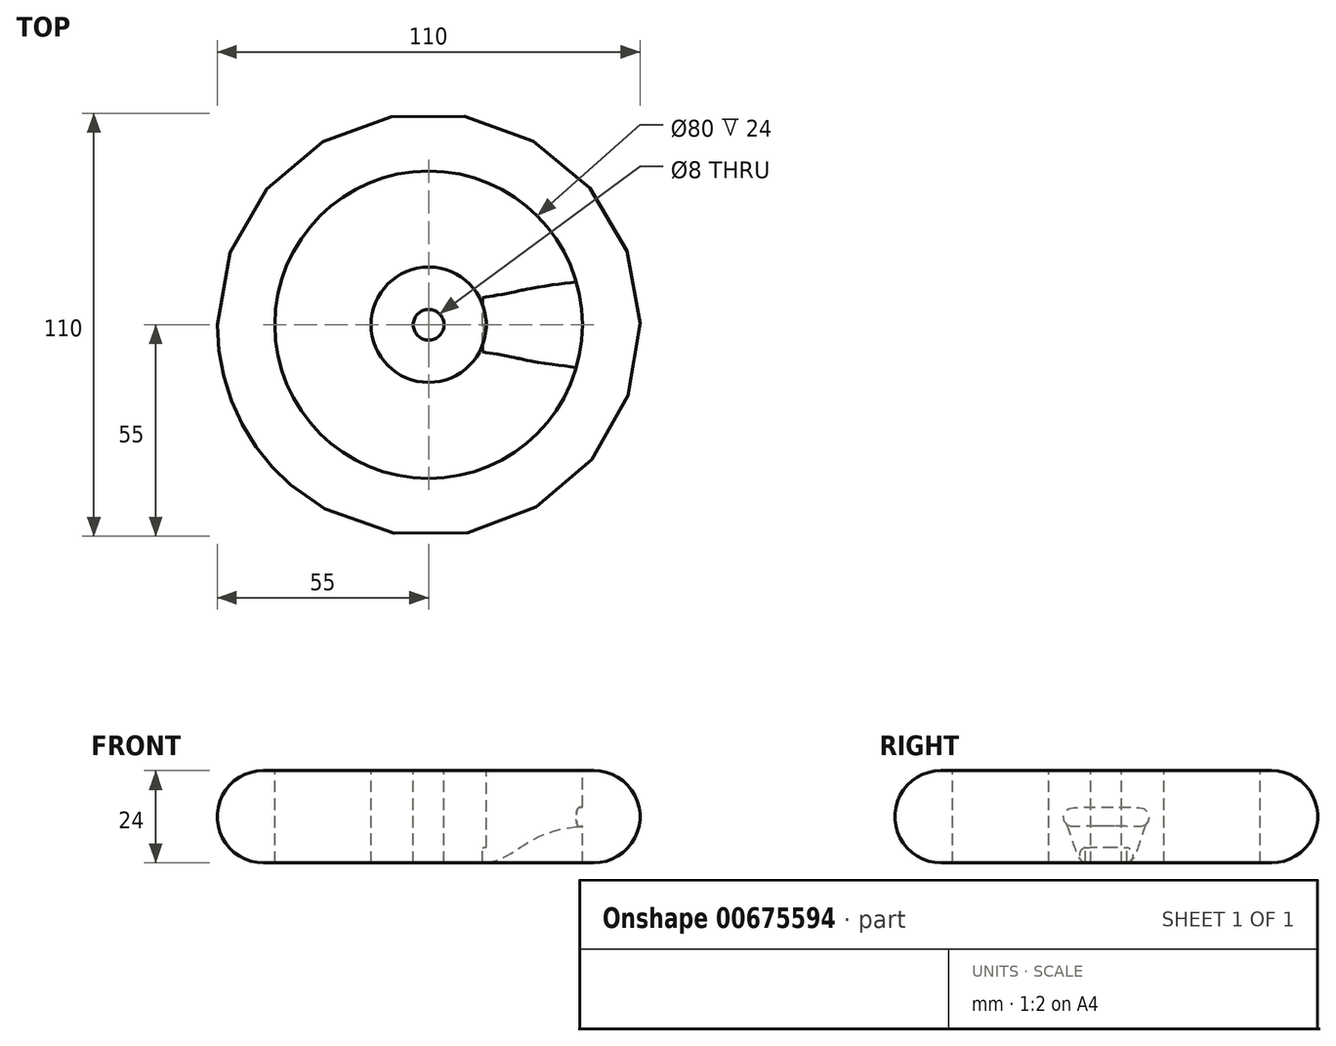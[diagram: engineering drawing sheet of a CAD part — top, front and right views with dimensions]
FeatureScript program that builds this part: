
annotation { "Feature Type Name" : "Feature", "Feature Type Description" : "" }
export const myFeature = defineFeature(function(context is Context, id is Id, definition is map)
    precondition{}
    {
        {
            var Q0;
            Q0=qCreatedBy(makeId("Top.planeOp"),FACE);
            var sketch = newSketch(context, id + "F0", { "sketchPlane" : qUnion([Q0])});
            skCircle(sketch, "E0", {"center": v(0, 0) * mm, "radius": 40 * mm});
            skSolve(sketch);
        }
        {
            var Q0;
            Q0=qCreatedBy(makeId("Front.planeOp"),FACE);
            var sketch = newSketch(context, id + "F1", { "sketchPlane" : qUnion([Q0])});
            skArc(sketch, "E1", {"start": v(-43, 12) * mm, "mid": v(-55, 0) * mm, "end": v(-43, -12) * mm});
            skLineSegment(sketch, "E2", {"start": v(-43, 12) * mm, "end": v(-40, 12) * mm});
            skLineSegment(sketch, "E3", {"start": v(-40, 12) * mm, "end": v(-40, -12) * mm});
            skLineSegment(sketch, "E4", {"start": v(-40, -12) * mm, "end": v(-43, -12) * mm});
            skSolve(sketch);
        }
        {
            var Q0;
            Q0 = qSketchRegion(id + "F1", true);
            var Q1;
            Q1=sQuery(id+"F0.wireOp",EDGE,"E0");
            sweep(context, id + "F2", {"profiles" : qUnion([Q0]), "path" : qUnion([Q1])});
        }
        {
            var Q0;
            Q0=qCreatedBy(makeId("Right.planeOp"),FACE);
            cPlane(context, id + "F3", {"entities" : qUnion([Q0]), "cplaneType" : CPlaneType.OFFSET, "offset" : 40 * mm, "width" : 150 * mm, "height" : 150 * mm});
        }
        {
            var Q0;
            Q0=qCreatedBy(id+"F3.planeOp",FACE);
            var sketch = newSketch(context, id + "F4", { "sketchPlane" : qUnion([Q0])});
            skLineSegment(sketch, "E5", {"start": v(9, 0) * mm, "end": v(-9, 0) * mm});
            skArc(sketch, "E6.0.startCap", {"start": v(9, 2.5) * mm, "mid": v(11.5, 0) * mm, "end": v(9, -2.5) * mm});
            skArc(sketch, "E6.0.endCap", {"start": v(-9, -2.5) * mm, "mid": v(-11.5, 0) * mm, "end": v(-9, 2.5) * mm});
            skLineSegment(sketch, "E6.0.left", {"start": v(9, -2.5) * mm, "end": v(-9, -2.5) * mm});
            skLineSegment(sketch, "E6.0.right", {"start": v(9, 2.5) * mm, "end": v(-9, 2.5) * mm});
            skSolve(sketch);
        }
        {
            var Q0;
            Q0=qCreatedBy(makeId("Right.planeOp"),FACE);
            cPlane(context, id + "F5", {"entities" : qUnion([Q0]), "cplaneType" : CPlaneType.OFFSET, "offset" : 14 * mm, "width" : 150 * mm, "height" : 150 * mm});
        }
        {
            var Q0;
            Q0=qCreatedBy(id+"F5.planeOp",FACE);
            var sketch = newSketch(context, id + "F6", { "sketchPlane" : qUnion([Q0])});
            skLineSegment(sketch, "E7", {"start": v(-5, -10) * mm, "end": v(5, -10) * mm});
            skArc(sketch, "E8.0.startCap", {"start": v(-5, -12) * mm, "mid": v(-7, -10) * mm, "end": v(-5, -8) * mm});
            skArc(sketch, "E8.0.endCap", {"start": v(5, -8) * mm, "mid": v(7, -10) * mm, "end": v(5, -12) * mm});
            skLineSegment(sketch, "E8.0.left", {"start": v(-5, -8) * mm, "end": v(5, -8) * mm});
            skLineSegment(sketch, "E8.0.right", {"start": v(-5, -12) * mm, "end": v(5, -12) * mm});
            skSolve(sketch);
        }
        {
            var Q0;
            Q0=qCreatedBy(makeId("Front.planeOp"),FACE);
            var sketch = newSketch(context, id + "F7", { "sketchPlane" : qUnion([Q0])});
            skFitSpline(sketch, "E9", {"points": [v(14, -12) * mm, v(19.07, -10.76) * mm, v(22.96, -8.5) * mm, v(26.93, -6.1) * mm, v(33.8, -3.4) * mm, v(40, -2.5) * mm], "startDerivative": vector(18.33, -0.52) * mm, "endDerivative": vector(12.15, -0.2) * mm});
            skSolve(sketch);
        }
        {
            var Q1;
            Q1 = qSketchRegion(id + "F6", true);
            var Q2;
            Q2 = qSketchRegion(id + "F4", true);
            var Q3;
            Q3 = qConstructionFilter(qBodyType(qCreatedBy(id + "F7" ,EDGE), BodyType.WIRE), ConstructionObject.NO);
            loft(context, id + "F8", {"operationType" : NewBodyOperationType.ADD, "addGuides" : true, "sheetProfilesArray" : [{ "sheetProfileEntities" : qUnion([Q1]) }, { "sheetProfileEntities" : qUnion([Q2]) }], "guidesArray" : [{ "guideEntities" : qUnion([Q3]), "guideDerivativeType" : LoftGuideDerivativeType.DEFAULT, "guideDerivativeMagnitude" : 1 }]});
        }
        {
            var Q0;
            Q0=qCreatedBy(makeId("Front.planeOp"),FACE);
            var sketch = newSketch(context, id + "F9", { "sketchPlane" : qUnion([Q0])});
            skLineSegment(sketch, "E10.bottom", {"start": v(0, 12) * mm, "end": v(15, 12) * mm});
            skLineSegment(sketch, "E10.top", {"start": v(0, -12) * mm, "end": v(15, -12) * mm});
            skLineSegment(sketch, "E10.left", {"start": v(0, 12) * mm, "end": v(0, -12) * mm});
            skLineSegment(sketch, "E10.right", {"start": v(15, 12) * mm, "end": v(15, -12) * mm});
            skSolve(sketch);
        }
        {
            var Q0;
            Q0 = qSketchRegion(id + "F9", true);
            var Q1;
            Q1=sQuery(id+"F9.wireOp",EDGE,"E10.left");
            revolve(context, id + "F10", {"operationType" : NewBodyOperationType.ADD, "surfaceOperationType" : NewSurfaceOperationType.NEW, "entities" : qUnion([Q0]), "axis" : qUnion([Q1]), "revolveType" : RevolveType.FULL});
        }
        {
            var Q0;
            Q0=makeQuery(id+"F10.opRevolve","SWEPT_FACE",FACE,{"disambiguationData":[OSD([sQuery(id+"F9.wireOp",EDGE,"E10.bottom")])]});
            var sketch = newSketch(context, id + "F11", { "sketchPlane" : qUnion([Q0])});
            skPoint(sketch, "E11", {"position": v(0, 0) * mm});
            skSolve(sketch);
        }
        {
            var Q0;
            Q0=sQuery(id+"F11.wireOp",VERTEX,"E11");
            var Q1;
            Q1=makeQuery(id+"F2.opSweep","SWEPT_BODY",BODY,{"disambiguationData":[OSD([sQuery(id+"F0.wireOp",EDGE,"E0"),sQuery(id+"F1.wireOp",EDGE,"E1"),sQuery(id+"F1.wireOp",EDGE,"E2"),sQuery(id+"F1.wireOp",EDGE,"E3"),sQuery(id+"F1.wireOp",EDGE,"E4")])]});
            hole(context, id + "F12", {"style" : HoleStyle.SIMPLE, "endStyle" : HoleEndStyle.THROUGH, "holeDiameter" : 8 * mm, "majorDiameter" : 5 * mm, "isTappedThrough" : true, "tappedDepth" : 12 * mm, "tapClearance" : 3, "locations" : qUnion([Q0]), "scope" : qUnion([Q1])});
        }
    });
